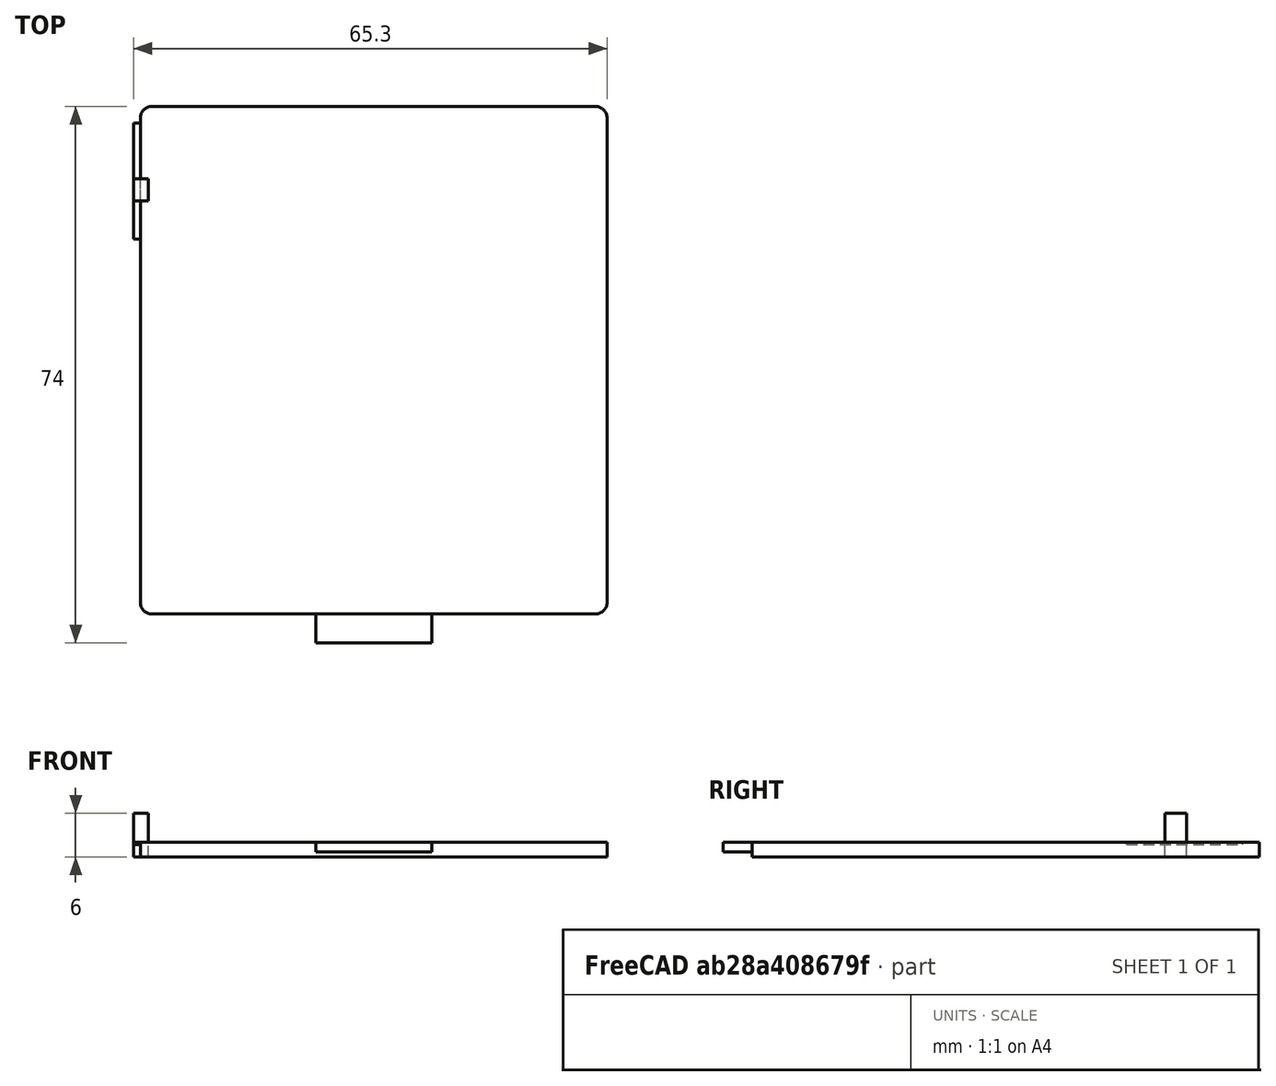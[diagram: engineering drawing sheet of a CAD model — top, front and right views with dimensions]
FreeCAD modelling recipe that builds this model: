
FCSTD DOCUMENT  (FreeCAD 0.21R33771 (Git))
Label: battery-lid
License: All rights reserved
LicenseURL: http://en.wikipedia.org/wiki/All_rights_reserved
objects: Part::Box×4, Part::Mirroring×2, Part::Fillet×1
note: 7 computed .brp shape members not serialized (recipe doc carries the construction recipe); baked Part::Feature solids carry a one-line shape summary decoded from their .brp

FEATURE [Part::Box] Box  label="Cube"
  AttacherType = Attacher::AttachEngine3D
  Height = 2
  Length = 64.4
  Placement = pos=(-32.2,0,0) rot=(0,0,1;0rad)
  Width = 70
FEATURE [Part::Box] Box001  label="Cube001"
  AttacherType = Attacher::AttachEngine3D
  Height = 1.3
  Length = 16
  Placement = pos=(-8,-4,0.7) rot=(0,0,1;0rad)
  Width = 4
FEATURE [Part::Box] Box002  label="Cube002"
  AttacherType = Attacher::AttachEngine3D
  Height = 0.3
  Length = 0.9
  Placement = pos=(32.2,51.7,1.7) rot=(0,0,1;0rad)
  Width = 16
FEATURE [Part::Box] Box003  label="Cube003"
  AttacherType = Attacher::AttachEngine3D
  Height = 6
  Length = 2
  Placement = pos=(31.1,57,0) rot=(0,0,1;0rad)
  Width = 3
FEATURE [Part::Fillet] Fillet
  Base = -> Box
  Edges = 4 edges r=1.6: [Edge1,Edge3,Edge5,Edge7]
FEATURE [Part::Mirroring] Part__Mirroring  label="Cube002 (Mirror #1)"
  Base = (0,0,0)
  Normal = (1,0,0)
  Source = -> Box002
FEATURE [Part::Mirroring] Part__Mirroring001  label="Cube003 (Mirror #2)"
  Base = (0,0,0)
  Normal = (1,0,0)
  Source = -> Box003
